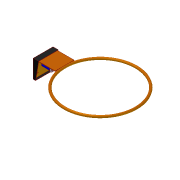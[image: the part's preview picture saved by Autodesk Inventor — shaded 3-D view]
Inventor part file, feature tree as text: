
AUTODESK INVENTOR PART (.ipt)
format: ipt  version: 2012 (Build 160160000, 160)  size: 231,424 bytes
history: native  units: in
note: dims shown in document units (in); Inventor stores cm internally (conversion verified against a paired STEP export)
features: sketch x9, extrude x8, hole x2, revolve x1, pattern_linear x1
ambient origin geometry x8: Origin, YZ Plane, XZ Plane, XY Plane, X Axis, Y Axis, Z Axis, Center Point
bodies: Solid1 (feature_tree)
feature tree (21):
  revolve  "Revolution1"  [1 undecoded]
  extrude  "Extrusion1"  TaperAngle=0.0deg  [1 undecoded]
  sketch  "Sketch3"  dims[d6=0.3125in d7=0.125in]
  hole  "Hole1"  [1 undecoded]
  pattern_linear  "Rectangular Pattern1"  Count1=2 Spacing1=3.1875in
  hole  "Hole2"  [1 undecoded]
  sketch  "Sketch4"  dims[d8=0.125in]
  extrude  "Extrusion2"  Depth=2.188in
  extrude  "Extrusion3"  Depth=3.4375in
  sketch  "Sketch8"  dims[d27=4.5in d28=5.5625in]
  extrude  "Extrusion7"  Depth=1.8125in
  extrude  "Extrusion4"  Depth=0.6875in
  extrude  "Extrusion5"  Depth=0.375in
  extrude  "Extrusion6"  Depth=0.5in
  extrude  "Extrusion8"  Depth=0.375in
  sketch  "Sketch1"  dims[d0=9.0in d1=0.625in]
  sketch  "Sketch2"  dims[d2=90.0deg d5=0.0in]
  sketch  "Sketch5"  dims[d9=0.25in]
  sketch  "Sketch6"  dims[d10=4.9375in d11=0.0in]
  sketch  "Sketch7"  dims[d12=0.875in d13=0.9063in d14=0.265in d15=0.75in d16=0.375in d17=0.25in d18=0.5635in d19=1.0in d20=0.8108in d21=0.7874in d23=3.1875in d24=0.7874in d26=2.625in]
  sketch  "Sketch9"  dims[d29=4.1875in d30=2.188in d31=3.4375in d32=1.8125in d33=0.6875in d34=0.375in d35=0.5in d36=0.375in d37=1.3125in d38=3.125in d39=1.3748in d40=2.5in d41=2.25in d42=0.5in d43=0.75in d44=0.375in d45=0.25in d46=0.5635in d47=1.0in d48=0.8108in d49=0.125in d50=0.125in d51=0.125in d52=0.125in d53=0.0625in d54=0.0625in d55=0.0in d56=1.3125in d57=0.0in d58=0.375in d59=2.375in d60=0.0in d61=1.5in d62=0.075in d63=0.0in d64=0.75in d65=0.25in d66=0.0in d67=0.25in d68=0.625in d69=0.25in d70=0.0in d71=1.1875in d72=0.6875in d73=2.25in d74=0.0in]
note: 4 required parameter values undecoded (feature->parameter linkage not recoverable at this tier; creation-order binding heuristic only, values carry confidence <= 0.55)